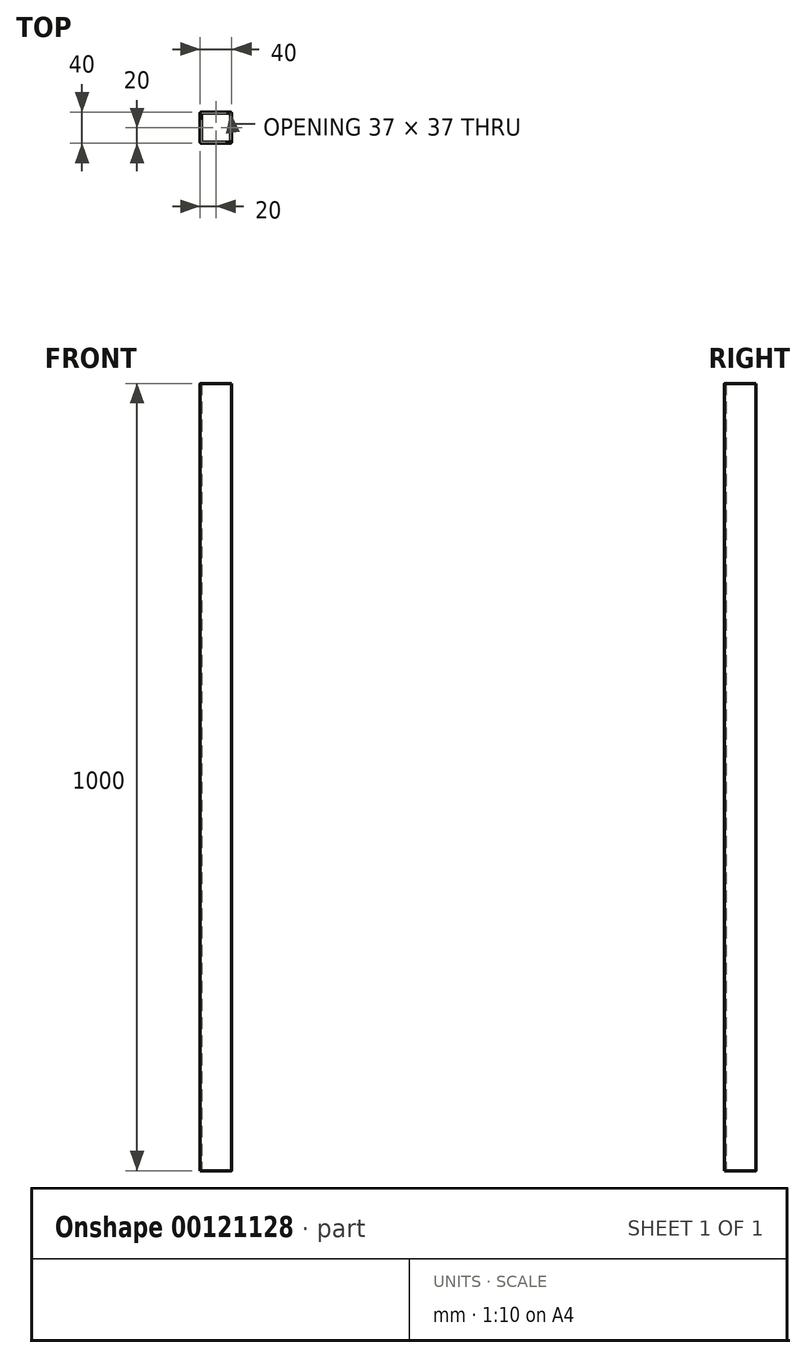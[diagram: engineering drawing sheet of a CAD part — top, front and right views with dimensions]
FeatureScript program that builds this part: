
annotation { "Feature Type Name" : "Feature", "Feature Type Description" : "" }
export const myFeature = defineFeature(function(context is Context, id is Id, definition is map)
    precondition{}
    {
        {
            var Q0;
            Q0=qCreatedBy(makeId("Top.planeOp"),FACE);
            var sketch = newSketch(context, id + "F0", { "sketchPlane" : qUnion([Q0])});
            skLineSegment(sketch, "E0.bottom", {"start": v(18, -20) * mm, "end": v(-18, -20) * mm});
            skLineSegment(sketch, "E0.top", {"start": v(18, 20) * mm, "end": v(-18, 20) * mm});
            skLineSegment(sketch, "E0.left", {"start": v(20, -18) * mm, "end": v(20, 18) * mm});
            skLineSegment(sketch, "E0.right", {"start": v(-20, -18) * mm, "end": v(-20, 18) * mm});
            skPoint(sketch, "E0.middle", {"position": v(0, 0) * mm});
            skPoint(sketch, "E1.visualSharp", {"position": v(-20, 20) * mm});
            skArc(sketch, "E1.filletArc", {"start": v(-18, 20) * mm, "mid": v(-19.41, 19.41) * mm, "end": v(-20, 18) * mm});
            skPoint(sketch, "E2.visualSharp", {"position": v(20, 20) * mm});
            skArc(sketch, "E2.filletArc", {"start": v(20, 18) * mm, "mid": v(19.41, 19.41) * mm, "end": v(18, 20) * mm});
            skPoint(sketch, "E3.visualSharp", {"position": v(20, -20) * mm});
            skArc(sketch, "E3.filletArc", {"start": v(18, -20) * mm, "mid": v(19.41, -19.41) * mm, "end": v(20, -18) * mm});
            skPoint(sketch, "E4.visualSharp", {"position": v(-20, -20) * mm});
            skArc(sketch, "E4.filletArc", {"start": v(-20, -18) * mm, "mid": v(-19.41, -19.41) * mm, "end": v(-18, -20) * mm});
            skPoint(sketch, "E5.visualSharp", {"position": v(-18.5, 18.5) * mm});
            skArc(sketch, "E6.0", {"start": v(18, -18.5) * mm, "mid": v(18.35, -18.35) * mm, "end": v(18.5, -18) * mm});
            skLineSegment(sketch, "E6.1", {"start": v(18.5, -18) * mm, "end": v(18.5, 18) * mm});
            skLineSegment(sketch, "E6.2", {"start": v(18, -18.5) * mm, "end": v(-18, -18.5) * mm});
            skArc(sketch, "E6.3", {"start": v(18.5, 18) * mm, "mid": v(18.35, 18.35) * mm, "end": v(18, 18.5) * mm});
            skArc(sketch, "E6.4", {"start": v(-18.5, -18) * mm, "mid": v(-18.35, -18.35) * mm, "end": v(-18, -18.5) * mm});
            skLineSegment(sketch, "E6.5", {"start": v(-18.5, -18) * mm, "end": v(-18.5, 18) * mm});
            skArc(sketch, "E6.6", {"start": v(-18, 18.5) * mm, "mid": v(-18.35, 18.35) * mm, "end": v(-18.5, 18) * mm});
            skLineSegment(sketch, "E6.7", {"start": v(18, 18.5) * mm, "end": v(-18, 18.5) * mm});
            skSolve(sketch);
        }
        {
            var Q0;
            Q0=makeQuery(id+"F0.imprint","IMPRINT",FACE,{"disambiguationData":[TD([[makeQuery(id+"F0.imprint","IMPRINT",EDGE,{"derivedFrom":sQuery(id+"F0.wireOp",EDGE,"E0.bottom")}),-1.0]])]});
            extrude(context, id + "F1", {"entities" : qUnion([Q0]), "depth" : 1000 * mm});
        }
    });
